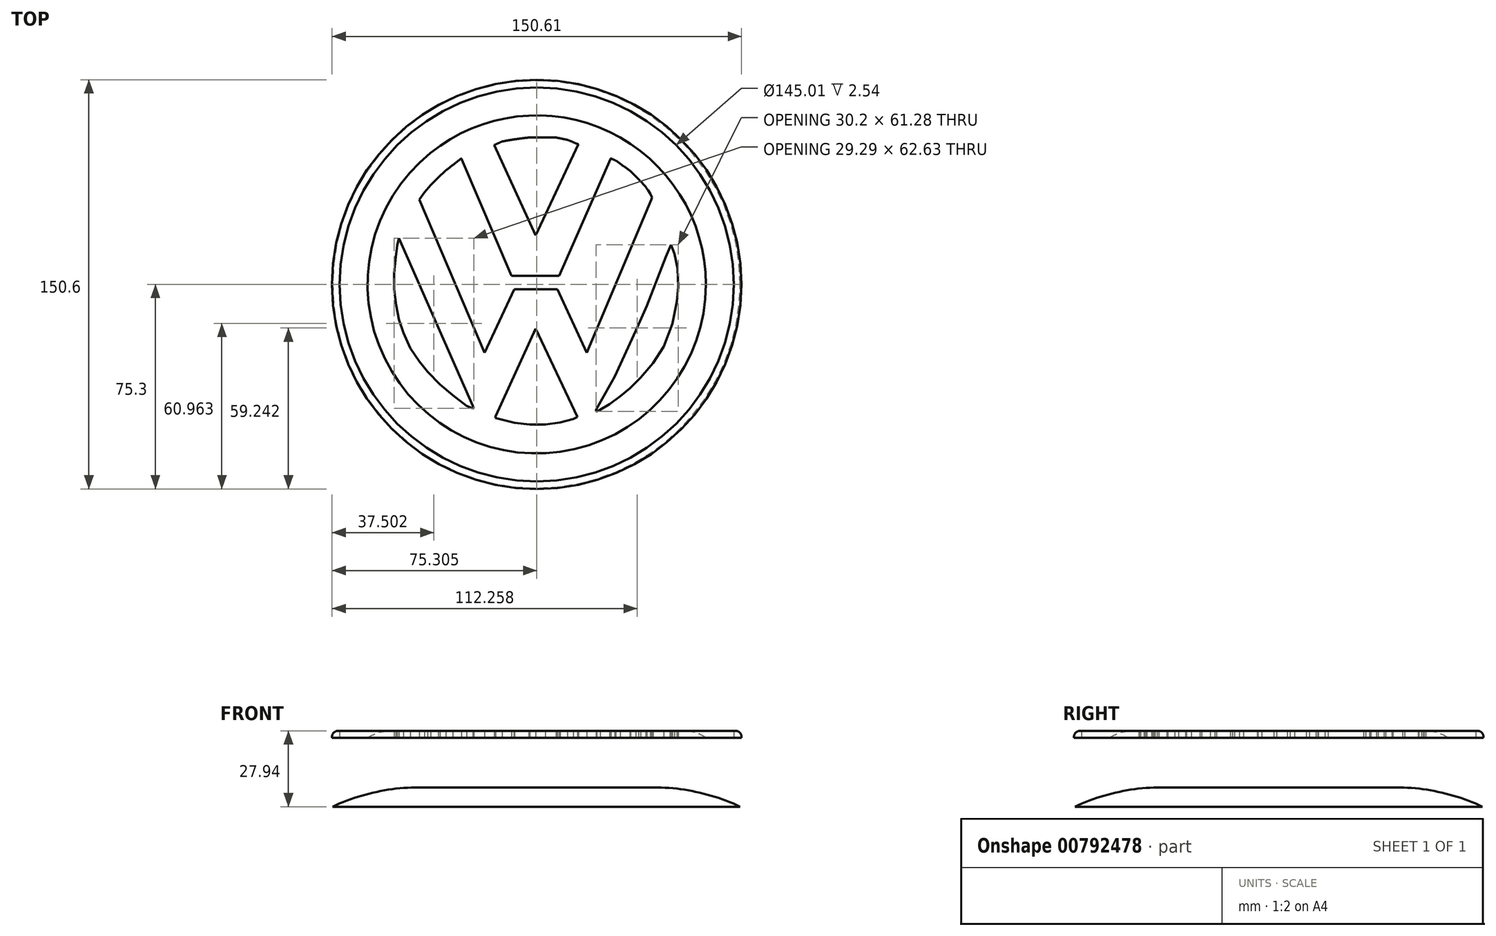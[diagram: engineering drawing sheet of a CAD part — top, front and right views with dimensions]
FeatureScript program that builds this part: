
annotation { "Feature Type Name" : "Feature", "Feature Type Description" : "" }
export const myFeature = defineFeature(function(context is Context, id is Id, definition is map)
    precondition{}
    {
        {
            var Q0;
            Q0=qCreatedBy(makeId("Top.planeOp"),FACE);
            cPlane(context, id + "F0", {"entities" : qUnion([Q0]), "cplaneType" : CPlaneType.OFFSET, "offset" : 25.4 * mm, "width" : 152.4 * mm, "height" : 152.4 * mm});
        }
        {
            var Q0;
            Q0=qCreatedBy(id+"F0.planeOp",FACE);
            var sketch = newSketch(context, id + "F1", { "sketchPlane" : qUnion([Q0])});
            skCircle(sketch, "E0", {"center": v(56.48, 0) * mm, "radius": 74.95 * mm});
            skSolve(sketch);
        }
        {
            var Q0;
            Q0 = qSketchRegion(id + "F1", true);
            extrude(context, id + "F2", {"entities" : qUnion([Q0]), "depth" : 7.11 * mm, "offsetDistance" : 25.4 * mm});
        }
        {
            var Q0;
            Q0=makeQuery(id+"F2.opExtrude","CAP_EDGE",EDGE,{"disambiguationData":[OSD([sQuery(id+"F1.wireOp",EDGE,"E0")])],"isStart":false});
            fillet(context, id + "F3", {"entities" : qUnion([Q0]), "radius" : 74.93 * mm, "tangentPropagation" : true, "allowEdgeOverflow" : false});
        }
        {
            var Q0;
            Q0=qCreatedBy(id+"F0.planeOp",FACE);
            cPlane(context, id + "F4", {"entities" : qUnion([Q0]), "cplaneType" : CPlaneType.OFFSET, "offset" : 25.4 * mm, "width" : 152.4 * mm, "height" : 152.4 * mm});
        }
        {
            var Q0;
            Q0=qCreatedBy(id+"F4.planeOp",FACE);
            var sketch = newSketch(context, id + "F5", { "sketchPlane" : qUnion([Q0])});
            skCircle(sketch, "E1", {"center": v(56.62, 0) * mm, "radius": 75.3 * mm});
            skCircle(sketch, "E2", {"center": v(56.62, 0) * mm, "radius": 72.5 * mm});
            skCircle(sketch, "E3", {"center": v(56.62, 0) * mm, "radius": 62.2 * mm});
            skLineSegment(sketch, "E4", {"start": v(13.39, 31.27) * mm, "end": v(37.38, -25.19) * mm});
            skLineSegment(sketch, "E5", {"start": v(37.38, -25.19) * mm, "end": v(48.34, -1.82) * mm});
            skLineSegment(sketch, "E6", {"start": v(48.34, -1.82) * mm, "end": v(64.27, -1.82) * mm});
            skLineSegment(sketch, "E7", {"start": v(64.27, -1.82) * mm, "end": v(75.02, -25.19) * mm});
            skLineSegment(sketch, "E8", {"start": v(75.02, -25.19) * mm, "end": v(98.8, 31.27) * mm});
            skLineSegment(sketch, "E9", {"start": v(28.9, 46.37) * mm, "end": v(47.28, 3.1) * mm});
            skLineSegment(sketch, "E10", {"start": v(47.28, 3.1) * mm, "end": v(64.89, 3.1) * mm});
            skLineSegment(sketch, "E11", {"start": v(64.89, 3.1) * mm, "end": v(83.92, 46.37) * mm});
            skLineSegment(sketch, "E12", {"start": v(13.39, 31.27) * mm, "end": v(15.32, 33.91) * mm});
            skLineSegment(sketch, "E13", {"start": v(15.32, 33.91) * mm, "end": v(17.67, 36.52) * mm});
            skLineSegment(sketch, "E14", {"start": v(17.67, 36.52) * mm, "end": v(20.36, 39.39) * mm});
            skLineSegment(sketch, "E15", {"start": v(20.36, 39.39) * mm, "end": v(23.23, 42) * mm});
            skLineSegment(sketch, "E16", {"start": v(23.23, 42) * mm, "end": v(26.36, 44.43) * mm});
            skLineSegment(sketch, "E17", {"start": v(26.36, 44.43) * mm, "end": v(28.9, 46.37) * mm});
            skLineSegment(sketch, "E18", {"start": v(71.93, 51.56) * mm, "end": v(56.28, 18.08) * mm});
            skLineSegment(sketch, "E19", {"start": v(56.28, 18.08) * mm, "end": v(40.97, 51.3) * mm});
            skLineSegment(sketch, "E20", {"start": v(40.97, 51.3) * mm, "end": v(43.84, 52.62) * mm});
            skLineSegment(sketch, "E21", {"start": v(43.84, 52.62) * mm, "end": v(48.28, 53.4) * mm});
            skLineSegment(sketch, "E22", {"start": v(48.28, 53.4) * mm, "end": v(53.67, 54.09) * mm});
            skLineSegment(sketch, "E23", {"start": v(53.67, 54.09) * mm, "end": v(58.63, 54.09) * mm});
            skLineSegment(sketch, "E24", {"start": v(58.63, 54.09) * mm, "end": v(63.67, 54.09) * mm});
            skLineSegment(sketch, "E25", {"start": v(63.67, 54.09) * mm, "end": v(67.93, 53.22) * mm});
            skLineSegment(sketch, "E26", {"start": v(67.93, 53.22) * mm, "end": v(71.93, 51.56) * mm});
            skLineSegment(sketch, "E27", {"start": v(83.92, 46.37) * mm, "end": v(85.74, 45.57) * mm});
            skLineSegment(sketch, "E28", {"start": v(85.74, 45.57) * mm, "end": v(88.15, 43.83) * mm});
            skLineSegment(sketch, "E29", {"start": v(88.15, 43.83) * mm, "end": v(91.15, 41.66) * mm});
            skLineSegment(sketch, "E30", {"start": v(91.15, 41.66) * mm, "end": v(94.05, 38.77) * mm});
            skLineSegment(sketch, "E31", {"start": v(94.05, 38.77) * mm, "end": v(96.68, 35.92) * mm});
            skLineSegment(sketch, "E32", {"start": v(96.68, 35.92) * mm, "end": v(98.34, 33.39) * mm});
            skLineSegment(sketch, "E33", {"start": v(98.34, 33.39) * mm, "end": v(98.98, 31.98) * mm});
            skLineSegment(sketch, "E34", {"start": v(98.98, 31.98) * mm, "end": v(98.8, 31.27) * mm});
            skLineSegment(sketch, "E35", {"start": v(5.9, 16.98) * mm, "end": v(33.09, -44.68) * mm});
            skLineSegment(sketch, "E36", {"start": v(33.09, -44.68) * mm, "end": v(33.46, -45.48) * mm});
            skLineSegment(sketch, "E37", {"start": v(33.46, -45.48) * mm, "end": v(33.09, -45.65) * mm});
            skLineSegment(sketch, "E38", {"start": v(33.09, -45.65) * mm, "end": v(30.87, -44.68) * mm});
            skLineSegment(sketch, "E39", {"start": v(30.87, -44.68) * mm, "end": v(25.7, -40.84) * mm});
            skLineSegment(sketch, "E40", {"start": v(25.7, -40.84) * mm, "end": v(21.02, -36.89) * mm});
            skLineSegment(sketch, "E41", {"start": v(21.02, -36.89) * mm, "end": v(16.45, -32.17) * mm});
            skLineSegment(sketch, "E42", {"start": v(16.45, -32.17) * mm, "end": v(13.39, -28.33) * mm});
            skLineSegment(sketch, "E43", {"start": v(13.39, -28.33) * mm, "end": v(10.15, -23.5) * mm});
            skLineSegment(sketch, "E44", {"start": v(10.15, -23.5) * mm, "end": v(7.55, -17.85) * mm});
            skLineSegment(sketch, "E45", {"start": v(7.55, -17.85) * mm, "end": v(5.98, -13.02) * mm});
            skLineSegment(sketch, "E46", {"start": v(5.98, -13.02) * mm, "end": v(4.86, -7.69) * mm});
            skLineSegment(sketch, "E47", {"start": v(4.86, -7.69) * mm, "end": v(4.17, -1.82) * mm});
            skLineSegment(sketch, "E48", {"start": v(4.17, -1.82) * mm, "end": v(4.17, 4.2) * mm});
            skLineSegment(sketch, "E49", {"start": v(4.17, 4.2) * mm, "end": v(4.75, 10.09) * mm});
            skLineSegment(sketch, "E50", {"start": v(4.75, 10.09) * mm, "end": v(5.23, 14.34) * mm});
            skLineSegment(sketch, "E51", {"start": v(5.23, 14.34) * mm, "end": v(5.9, 16.98) * mm});
            skLineSegment(sketch, "E52", {"start": v(78.5, -46.17) * mm, "end": v(85.3, -33.95) * mm});
            skLineSegment(sketch, "E53", {"start": v(85.3, -33.95) * mm, "end": v(93.07, -17) * mm});
            skLineSegment(sketch, "E54", {"start": v(93.07, -17) * mm, "end": v(97.08, -7.9) * mm});
            skLineSegment(sketch, "E55", {"start": v(97.08, -7.9) * mm, "end": v(101.11, 2.26) * mm});
            skLineSegment(sketch, "E56", {"start": v(101.11, 2.26) * mm, "end": v(104.14, 10.09) * mm});
            skLineSegment(sketch, "E57", {"start": v(104.14, 10.09) * mm, "end": v(105.57, 13.73) * mm});
            skLineSegment(sketch, "E58", {"start": v(105.57, 13.73) * mm, "end": v(105.95, 14.58) * mm});
            skLineSegment(sketch, "E59", {"start": v(105.95, 14.58) * mm, "end": v(107.33, 11.33) * mm});
            skLineSegment(sketch, "E60", {"start": v(107.33, 11.33) * mm, "end": v(108.44, 5.78) * mm});
            skLineSegment(sketch, "E61", {"start": v(108.44, 5.78) * mm, "end": v(108.67, -0.84) * mm});
            skLineSegment(sketch, "E62", {"start": v(108.67, -0.84) * mm, "end": v(108.13, -6.3) * mm});
            skLineSegment(sketch, "E63", {"start": v(108.13, -6.3) * mm, "end": v(106.56, -14.55) * mm});
            skLineSegment(sketch, "E64", {"start": v(106.56, -14.55) * mm, "end": v(103.39, -22.9) * mm});
            skLineSegment(sketch, "E65", {"start": v(103.39, -22.9) * mm, "end": v(99.35, -29.03) * mm});
            skLineSegment(sketch, "E66", {"start": v(99.35, -29.03) * mm, "end": v(94.9, -34.3) * mm});
            skLineSegment(sketch, "E67", {"start": v(94.9, -34.3) * mm, "end": v(90.87, -38.2) * mm});
            skLineSegment(sketch, "E68", {"start": v(90.87, -38.2) * mm, "end": v(87.33, -41.2) * mm});
            skLineSegment(sketch, "E69", {"start": v(87.33, -41.2) * mm, "end": v(83.4, -44.04) * mm});
            skLineSegment(sketch, "E70", {"start": v(83.4, -44.04) * mm, "end": v(79.96, -46.14) * mm});
            skLineSegment(sketch, "E71", {"start": v(79.96, -46.14) * mm, "end": v(78.74, -46.7) * mm});
            skLineSegment(sketch, "E72", {"start": v(78.74, -46.7) * mm, "end": v(78.47, -46.58) * mm});
            skLineSegment(sketch, "E73", {"start": v(78.47, -46.58) * mm, "end": v(78.5, -46.17) * mm});
            skLineSegment(sketch, "E74", {"start": v(41.45, -48.5) * mm, "end": v(56.2, -16.3) * mm});
            skLineSegment(sketch, "E75", {"start": v(56.2, -16.3) * mm, "end": v(71.56, -48.8) * mm});
            skLineSegment(sketch, "E76", {"start": v(71.56, -48.8) * mm, "end": v(70.01, -49.53) * mm});
            skLineSegment(sketch, "E77", {"start": v(70.01, -49.53) * mm, "end": v(65.28, -50.87) * mm});
            skLineSegment(sketch, "E78", {"start": v(65.28, -50.87) * mm, "end": v(59.84, -51.5) * mm});
            skLineSegment(sketch, "E79", {"start": v(59.84, -51.5) * mm, "end": v(54.11, -51.5) * mm});
            skLineSegment(sketch, "E80", {"start": v(54.11, -51.5) * mm, "end": v(48.46, -50.89) * mm});
            skLineSegment(sketch, "E81", {"start": v(48.46, -50.89) * mm, "end": v(44.96, -50) * mm});
            skLineSegment(sketch, "E82", {"start": v(44.96, -50) * mm, "end": v(41.37, -49.1) * mm});
            skLineSegment(sketch, "E83", {"start": v(41.37, -49.1) * mm, "end": v(41.45, -48.5) * mm});
            skSolve(sketch);
        }
        {
            var Q0;
            Q0=makeQuery(id+"F5.imprint","IMPRINT",FACE,{"disambiguationData":[TD([[makeQuery(id+"F5.imprint","IMPRINT",EDGE,{"derivedFrom":sQuery(id+"F5.wireOp",EDGE,"E1")}),1.0]])]});
            var Q1;
            Q1=makeQuery(id+"F5.imprint","IMPRINT",FACE,{"disambiguationData":[TD([[makeQuery(id+"F5.imprint","IMPRINT",EDGE,{"derivedFrom":sQuery(id+"F5.wireOp",EDGE,"E3")}),1.0]])]});
            extrude(context, id + "F6", {"entities" : qUnion([Q0, Q1]), "depth" : 2.54 * mm, "offsetDistance" : 25.4 * mm});
        }
        {
            var Q0;
            Q0=makeQuery(id+"F6.opExtrude","CAP_EDGE",EDGE,{"disambiguationData":[OSD([sQuery(id+"F5.wireOp",EDGE,"E1")])],"isStart":false});
            fillet(context, id + "F7", {"entities" : qUnion([Q0]), "radius" : 2.2 * mm, "tangentPropagation" : true, "allowEdgeOverflow" : false});
        }
        {
            var Q0;
            Q0=makeQuery(id+"F6.opExtrude","CAP_EDGE",EDGE,{"disambiguationData":[OSD([sQuery(id+"F5.wireOp",EDGE,"E3")])],"isStart":false});
            fillet(context, id + "F8", {"entities" : qUnion([Q0]), "radius" : 15.76 * mm, "tangentPropagation" : true, "allowEdgeOverflow" : false});
        }
    });
